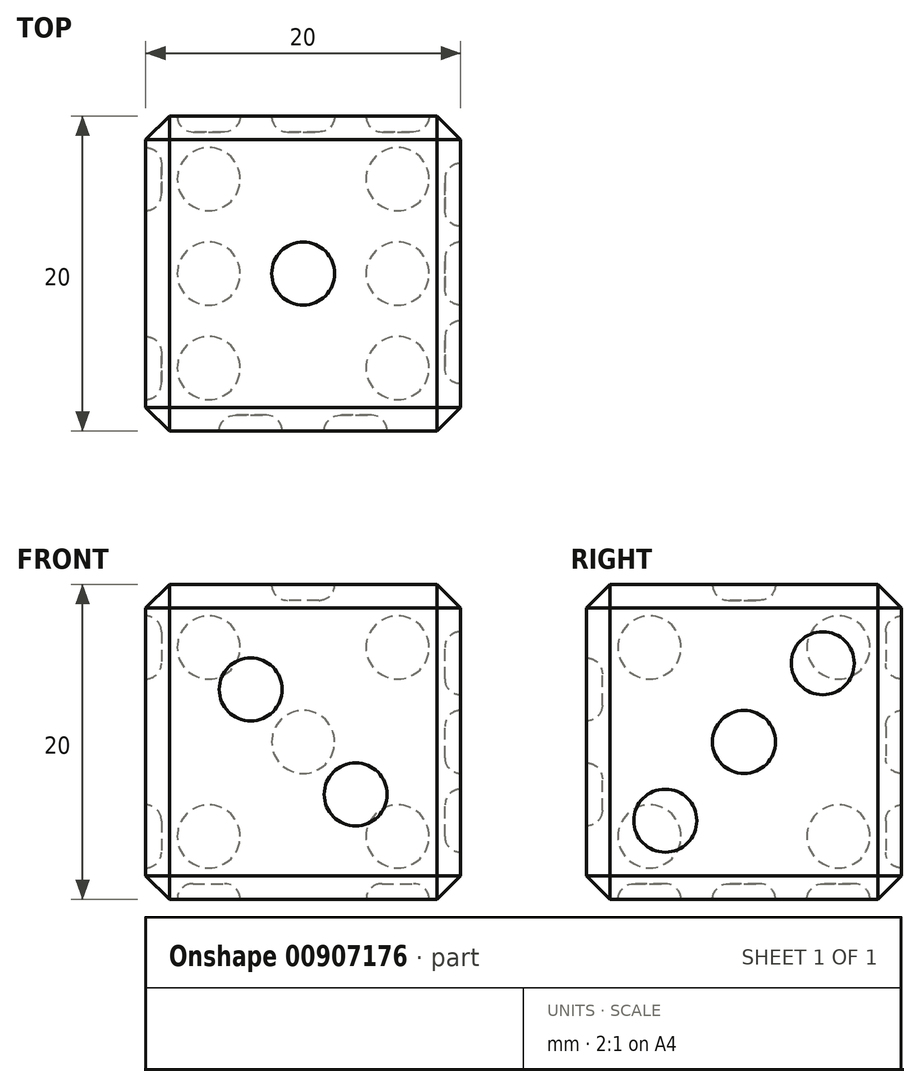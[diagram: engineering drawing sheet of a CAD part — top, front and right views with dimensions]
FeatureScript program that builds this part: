
annotation { "Feature Type Name" : "Feature", "Feature Type Description" : "" }
export const myFeature = defineFeature(function(context is Context, id is Id, definition is map)
    precondition{}
    {
        {
            var Q0;
            Q0=qCreatedBy(makeId("Top.planeOp"),FACE);
            var sketch = newSketch(context, id + "F0", { "sketchPlane" : qUnion([Q0])});
            skLineSegment(sketch, "E0.bottom", {"start": v(0, 0) * mm, "end": v(20, 0) * mm});
            skLineSegment(sketch, "E0.top", {"start": v(0, 20) * mm, "end": v(20, 20) * mm});
            skLineSegment(sketch, "E0.left", {"start": v(0, 0) * mm, "end": v(0, 20) * mm});
            skLineSegment(sketch, "E0.right", {"start": v(20, 0) * mm, "end": v(20, 20) * mm});
            skSolve(sketch);
        }
        {
            var Q0;
            Q0=makeQuery(id+"F0.imprint","IMPRINT",FACE,{"disambiguationData":[TD([[makeQuery(id+"F0.imprint","IMPRINT",EDGE,{"derivedFrom":sQuery(id+"F0.wireOp",EDGE,"E0.bottom")}),1.0]])]});
            extrude(context, id + "F1", {"entities" : qUnion([Q0]), "depth" : 20 * mm, "offsetDistance" : 25 * mm});
        }
        {
            var Q0;
            Q0=makeQuery(id+"F1.opExtrude","CAP_FACE",FACE,{"disambiguationData":[OSD([sQuery(id+"F0.wireOp",EDGE,"E0.bottom"),sQuery(id+"F0.wireOp",EDGE,"E0.top"),sQuery(id+"F0.wireOp",EDGE,"E0.left"),sQuery(id+"F0.wireOp",EDGE,"E0.right")])],"isStart":false});
            var sketch = newSketch(context, id + "F2", { "sketchPlane" : qUnion([Q0])});
            skLineSegment(sketch, "E1", {"start": v(0, 20) * mm, "end": v(20, 0) * mm, "construction": true});
            skLineSegment(sketch, "E2", {"start": v(20, 20) * mm, "end": v(0, 0) * mm, "construction": true});
            skCircle(sketch, "E3", {"center": v(10, 10) * mm, "radius": 2 * mm});
            skSolve(sketch);
        }
        {
            var Q0;
            Q0=makeQuery(id+"F1.opExtrude","CAP_FACE",FACE,{"disambiguationData":[OSD([sQuery(id+"F0.wireOp",EDGE,"E0.bottom"),sQuery(id+"F0.wireOp",EDGE,"E0.top"),sQuery(id+"F0.wireOp",EDGE,"E0.left"),sQuery(id+"F0.wireOp",EDGE,"E0.right")])],"isStart":true});
            var sketch = newSketch(context, id + "F3", { "sketchPlane" : qUnion([Q0])});
            skLineSegment(sketch, "E4", {"start": v(20, -20) * mm, "end": v(0, 0) * mm, "construction": true});
            skLineSegment(sketch, "E5", {"start": v(0, -20) * mm, "end": v(20, 0) * mm, "construction": true});
            skLineSegment(sketch, "E6.bottom", {"start": v(4, -16) * mm, "end": v(16, -16) * mm, "construction": true});
            skLineSegment(sketch, "E6.top", {"start": v(4, -4) * mm, "end": v(16, -4) * mm, "construction": true});
            skLineSegment(sketch, "E6.left", {"start": v(4, -16) * mm, "end": v(4, -4) * mm, "construction": true});
            skLineSegment(sketch, "E6.right", {"start": v(16, -16) * mm, "end": v(16, -4) * mm, "construction": true});
            skPoint(sketch, "E6.middle", {"position": v(10, -10) * mm});
            skCircle(sketch, "E7", {"center": v(4, -16) * mm, "radius": 2 * mm});
            skCircle(sketch, "E8", {"center": v(4, -4) * mm, "radius": 2 * mm});
            skCircle(sketch, "E9", {"center": v(16, -4) * mm, "radius": 2 * mm});
            skCircle(sketch, "E10", {"center": v(16, -16) * mm, "radius": 2 * mm});
            skCircle(sketch, "E11", {"center": v(16, -10) * mm, "radius": 2 * mm});
            skCircle(sketch, "E12", {"center": v(4, -10) * mm, "radius": 2 * mm});
            skSolve(sketch);
        }
        {
            var Q0;
            Q0=makeQuery(id+"F1.opExtrude","SWEPT_FACE",FACE,{"disambiguationData":[OSD([sQuery(id+"F0.wireOp",EDGE,"E0.bottom")])]});
            var sketch = newSketch(context, id + "F4", { "sketchPlane" : qUnion([Q0])});
            skCircle(sketch, "E13", {"center": v(6.67, 13.33) * mm, "radius": 2 * mm});
            skCircle(sketch, "E14", {"center": v(13.33, 6.67) * mm, "radius": 2 * mm});
            skLineSegment(sketch, "E15", {"start": v(20, 0) * mm, "end": v(13.33, 6.67) * mm, "construction": true});
            skLineSegment(sketch, "E16", {"start": v(13.33, 6.67) * mm, "end": v(6.67, 13.33) * mm, "construction": true});
            skLineSegment(sketch, "E17", {"start": v(6.67, 13.33) * mm, "end": v(0, 20) * mm, "construction": true});
            skSolve(sketch);
        }
        {
            var Q0;
            Q0=makeQuery(id+"F1.opExtrude","SWEPT_FACE",FACE,{"disambiguationData":[OSD([sQuery(id+"F0.wireOp",EDGE,"E0.top")])]});
            var sketch = newSketch(context, id + "F5", { "sketchPlane" : qUnion([Q0])});
            skLineSegment(sketch, "E18", {"start": v(0, 20) * mm, "end": v(-20, 0) * mm, "construction": true});
            skLineSegment(sketch, "E19", {"start": v(0, 0) * mm, "end": v(-20, 20) * mm, "construction": true});
            skLineSegment(sketch, "E20.bottom", {"start": v(-4, 16) * mm, "end": v(-16, 16) * mm, "construction": true});
            skLineSegment(sketch, "E20.top", {"start": v(-4, 4) * mm, "end": v(-16, 4) * mm, "construction": true});
            skLineSegment(sketch, "E20.left", {"start": v(-4, 16) * mm, "end": v(-4, 4) * mm, "construction": true});
            skLineSegment(sketch, "E20.right", {"start": v(-16, 16) * mm, "end": v(-16, 4) * mm, "construction": true});
            skPoint(sketch, "E20.middle", {"position": v(-10, 10) * mm});
            skCircle(sketch, "E21", {"center": v(-4, 16) * mm, "radius": 2 * mm});
            skCircle(sketch, "E22", {"center": v(-4, 4) * mm, "radius": 2 * mm});
            skCircle(sketch, "E23", {"center": v(-10, 10) * mm, "radius": 2 * mm});
            skCircle(sketch, "E24", {"center": v(-16, 16) * mm, "radius": 2 * mm});
            skCircle(sketch, "E25", {"center": v(-16, 4) * mm, "radius": 2 * mm});
            skSolve(sketch);
        }
        {
            var Q0;
            Q0=makeQuery(id+"F1.opExtrude","SWEPT_FACE",FACE,{"disambiguationData":[OSD([sQuery(id+"F0.wireOp",EDGE,"E0.right")])]});
            var sketch = newSketch(context, id + "F6", { "sketchPlane" : qUnion([Q0])});
            skCircle(sketch, "E26", {"center": v(15, 15) * mm, "radius": 2 * mm});
            skCircle(sketch, "E27", {"center": v(10, 10) * mm, "radius": 2 * mm});
            skCircle(sketch, "E28", {"center": v(5, 5) * mm, "radius": 2 * mm});
            skLineSegment(sketch, "E29", {"start": v(0, 0) * mm, "end": v(5, 5) * mm, "construction": true});
            skLineSegment(sketch, "E30", {"start": v(10, 10) * mm, "end": v(5, 5) * mm, "construction": true});
            skLineSegment(sketch, "E31", {"start": v(10, 10) * mm, "end": v(15, 15) * mm, "construction": true});
            skLineSegment(sketch, "E32", {"start": v(15, 15) * mm, "end": v(20, 20) * mm, "construction": true});
            skSolve(sketch);
        }
        {
            var Q0;
            Q0=makeQuery(id+"F1.opExtrude","SWEPT_FACE",FACE,{"disambiguationData":[OSD([sQuery(id+"F0.wireOp",EDGE,"E0.left")])]});
            var sketch = newSketch(context, id + "F7", { "sketchPlane" : qUnion([Q0])});
            skLineSegment(sketch, "E33", {"start": v(-20, 20) * mm, "end": v(0, 0) * mm, "construction": true});
            skLineSegment(sketch, "E34", {"start": v(0, 20) * mm, "end": v(-20, 0) * mm, "construction": true});
            skLineSegment(sketch, "E35.bottom", {"start": v(-16, 16) * mm, "end": v(-4, 16) * mm, "construction": true});
            skLineSegment(sketch, "E35.top", {"start": v(-16, 4) * mm, "end": v(-4, 4) * mm, "construction": true});
            skLineSegment(sketch, "E35.left", {"start": v(-16, 16) * mm, "end": v(-16, 4) * mm, "construction": true});
            skLineSegment(sketch, "E35.right", {"start": v(-4, 16) * mm, "end": v(-4, 4) * mm, "construction": true});
            skPoint(sketch, "E35.middle", {"position": v(-10, 10) * mm});
            skCircle(sketch, "E36", {"center": v(-16, 16) * mm, "radius": 2 * mm});
            skCircle(sketch, "E37", {"center": v(-16, 4) * mm, "radius": 2 * mm});
            skCircle(sketch, "E38", {"center": v(-4, 4) * mm, "radius": 2 * mm});
            skCircle(sketch, "E39", {"center": v(-4, 16) * mm, "radius": 2 * mm});
            skSolve(sketch);
        }
        {
            var Q0;
            Q0=makeQuery(id+"F5.imprint","IMPRINT",FACE,{"disambiguationData":[TD([[makeQuery(id+"F5.imprint","IMPRINT",EDGE,{"derivedFrom":sQuery(id+"F5.wireOp",EDGE,"E24")}),1.0]])]});
            var Q1;
            Q1=makeQuery(id+"F5.imprint","IMPRINT",FACE,{"disambiguationData":[TD([[makeQuery(id+"F5.imprint","IMPRINT",EDGE,{"derivedFrom":sQuery(id+"F5.wireOp",EDGE,"E21")}),1.0]])]});
            var Q2;
            Q2=makeQuery(id+"F5.imprint","IMPRINT",FACE,{"disambiguationData":[TD([[makeQuery(id+"F5.imprint","IMPRINT",EDGE,{"derivedFrom":sQuery(id+"F5.wireOp",EDGE,"E23")}),1.0]])]});
            var Q3;
            Q3=makeQuery(id+"F5.imprint","IMPRINT",FACE,{"disambiguationData":[TD([[makeQuery(id+"F5.imprint","IMPRINT",EDGE,{"derivedFrom":sQuery(id+"F5.wireOp",EDGE,"E22")}),1.0]])]});
            var Q4;
            Q4=makeQuery(id+"F5.imprint","IMPRINT",FACE,{"disambiguationData":[TD([[makeQuery(id+"F5.imprint","IMPRINT",EDGE,{"derivedFrom":sQuery(id+"F5.wireOp",EDGE,"E25")}),1.0]])]});
            extrude(context, id + "F8", {"entities" : qUnion([Q0, Q1, Q2, Q3, Q4]), "operationType" : NewBodyOperationType.REMOVE, "oppositeDirection" : true, "depth" : 1 * mm, "offsetDistance" : 25 * mm});
        }
        {
            var Q0;
            Q0=makeQuery(id+"F2.imprint","IMPRINT",FACE,{"disambiguationData":[TD([[makeQuery(id+"F2.imprint","IMPRINT",EDGE,{"derivedFrom":sQuery(id+"F2.wireOp",EDGE,"E3")}),1.0]])]});
            extrude(context, id + "F9", {"entities" : qUnion([Q0]), "operationType" : NewBodyOperationType.REMOVE, "oppositeDirection" : true, "depth" : 1 * mm, "offsetDistance" : 25 * mm});
        }
        {
            var Q0;
            Q0=makeQuery(id+"F3.imprint","IMPRINT",FACE,{"disambiguationData":[TD([[makeQuery(id+"F3.imprint","IMPRINT",EDGE,{"derivedFrom":sQuery(id+"F3.wireOp",EDGE,"E10")}),1.0]])]});
            var Q1;
            Q1=makeQuery(id+"F3.imprint","IMPRINT",FACE,{"disambiguationData":[TD([[makeQuery(id+"F3.imprint","IMPRINT",EDGE,{"derivedFrom":sQuery(id+"F3.wireOp",EDGE,"E11")}),1.0]])]});
            var Q2;
            Q2=makeQuery(id+"F3.imprint","IMPRINT",FACE,{"disambiguationData":[TD([[makeQuery(id+"F3.imprint","IMPRINT",EDGE,{"derivedFrom":sQuery(id+"F3.wireOp",EDGE,"E9")}),1.0]])]});
            var Q3;
            Q3=makeQuery(id+"F3.imprint","IMPRINT",FACE,{"disambiguationData":[TD([[makeQuery(id+"F3.imprint","IMPRINT",EDGE,{"derivedFrom":sQuery(id+"F3.wireOp",EDGE,"E8")}),1.0]])]});
            var Q4;
            Q4=makeQuery(id+"F3.imprint","IMPRINT",FACE,{"disambiguationData":[TD([[makeQuery(id+"F3.imprint","IMPRINT",EDGE,{"derivedFrom":sQuery(id+"F3.wireOp",EDGE,"E12")}),1.0]])]});
            var Q5;
            Q5=makeQuery(id+"F3.imprint","IMPRINT",FACE,{"disambiguationData":[TD([[makeQuery(id+"F3.imprint","IMPRINT",EDGE,{"derivedFrom":sQuery(id+"F3.wireOp",EDGE,"E7")}),1.0]])]});
            extrude(context, id + "F10", {"entities" : qUnion([Q0, Q1, Q2, Q3, Q4, Q5]), "operationType" : NewBodyOperationType.REMOVE, "oppositeDirection" : true, "depth" : 1 * mm, "offsetDistance" : 25 * mm});
        }
        {
            var Q0;
            Q0=makeQuery(id+"F7.imprint","IMPRINT",FACE,{"disambiguationData":[TD([[makeQuery(id+"F7.imprint","IMPRINT",EDGE,{"derivedFrom":sQuery(id+"F7.wireOp",EDGE,"E37")}),1.0]])]});
            var Q1;
            Q1=makeQuery(id+"F7.imprint","IMPRINT",FACE,{"disambiguationData":[TD([[makeQuery(id+"F7.imprint","IMPRINT",EDGE,{"derivedFrom":sQuery(id+"F7.wireOp",EDGE,"E36")}),1.0]])]});
            var Q2;
            Q2=makeQuery(id+"F7.imprint","IMPRINT",FACE,{"disambiguationData":[TD([[makeQuery(id+"F7.imprint","IMPRINT",EDGE,{"derivedFrom":sQuery(id+"F7.wireOp",EDGE,"E39")}),1.0]])]});
            var Q3;
            Q3=makeQuery(id+"F7.imprint","IMPRINT",FACE,{"disambiguationData":[TD([[makeQuery(id+"F7.imprint","IMPRINT",EDGE,{"derivedFrom":sQuery(id+"F7.wireOp",EDGE,"E38")}),1.0]])]});
            extrude(context, id + "F11", {"entities" : qUnion([Q0, Q1, Q2, Q3]), "operationType" : NewBodyOperationType.REMOVE, "oppositeDirection" : true, "depth" : 1 * mm, "offsetDistance" : 25 * mm});
        }
        {
            var Q0;
            Q0=makeQuery(id+"F4.imprint","IMPRINT",FACE,{"disambiguationData":[TD([[makeQuery(id+"F4.imprint","IMPRINT",EDGE,{"derivedFrom":sQuery(id+"F4.wireOp",EDGE,"E14")}),1.0]])]});
            var Q1;
            Q1=makeQuery(id+"F4.imprint","IMPRINT",FACE,{"disambiguationData":[TD([[makeQuery(id+"F4.imprint","IMPRINT",EDGE,{"derivedFrom":sQuery(id+"F4.wireOp",EDGE,"E13")}),1.0]])]});
            extrude(context, id + "F12", {"entities" : qUnion([Q0, Q1]), "operationType" : NewBodyOperationType.REMOVE, "oppositeDirection" : true, "depth" : 1 * mm, "offsetDistance" : 25 * mm});
        }
        {
            var Q0;
            Q0=makeQuery(id+"F6.imprint","IMPRINT",FACE,{"disambiguationData":[TD([[makeQuery(id+"F6.imprint","IMPRINT",EDGE,{"derivedFrom":sQuery(id+"F6.wireOp",EDGE,"E26")}),1.0]])]});
            var Q1;
            Q1=makeQuery(id+"F6.imprint","IMPRINT",FACE,{"disambiguationData":[TD([[makeQuery(id+"F6.imprint","IMPRINT",EDGE,{"derivedFrom":sQuery(id+"F6.wireOp",EDGE,"E27")}),1.0]])]});
            var Q2;
            Q2=makeQuery(id+"F6.imprint","IMPRINT",FACE,{"disambiguationData":[TD([[makeQuery(id+"F6.imprint","IMPRINT",EDGE,{"derivedFrom":sQuery(id+"F6.wireOp",EDGE,"E28")}),1.0]])]});
            extrude(context, id + "F13", {"entities" : qUnion([Q0, Q1, Q2]), "operationType" : NewBodyOperationType.REMOVE, "oppositeDirection" : true, "depth" : 1 * mm, "offsetDistance" : 25 * mm});
        }
        {
            var Q0;
            Q0=makeQuery(id+"F1.opExtrude","CAP_EDGE",EDGE,{"disambiguationData":[OSD([sQuery(id+"F0.wireOp",EDGE,"E0.right")])],"isStart":false});
            var Q1;
            Q1=makeQuery(id+"F1.opExtrude","SWEPT_EDGE",EDGE,{"disambiguationData":[OSD([sQuery(id+"F0.wireOp",EDGE,"E0.bottom"),sQuery(id+"F0.wireOp",EDGE,"E0.right")])]});
            var Q2;
            Q2=makeQuery(id+"F1.opExtrude","SWEPT_EDGE",EDGE,{"disambiguationData":[OSD([sQuery(id+"F0.wireOp",EDGE,"E0.top"),sQuery(id+"F0.wireOp",EDGE,"E0.right")])]});
            var Q3;
            Q3=makeQuery(id+"F1.opExtrude","CAP_EDGE",EDGE,{"disambiguationData":[OSD([sQuery(id+"F0.wireOp",EDGE,"E0.right")])],"isStart":true});
            var Q4;
            Q4=makeQuery(id+"F1.opExtrude","CAP_EDGE",EDGE,{"disambiguationData":[OSD([sQuery(id+"F0.wireOp",EDGE,"E0.bottom")])],"isStart":true});
            var Q5;
            Q5=makeQuery(id+"F1.opExtrude","CAP_EDGE",EDGE,{"disambiguationData":[OSD([sQuery(id+"F0.wireOp",EDGE,"E0.top")])],"isStart":true});
            var Q6;
            Q6=makeQuery(id+"F1.opExtrude","CAP_EDGE",EDGE,{"disambiguationData":[OSD([sQuery(id+"F0.wireOp",EDGE,"E0.left")])],"isStart":true});
            var Q7;
            Q7=makeQuery(id+"F1.opExtrude","SWEPT_EDGE",EDGE,{"disambiguationData":[OSD([sQuery(id+"F0.wireOp",EDGE,"E0.bottom"),sQuery(id+"F0.wireOp",EDGE,"E0.left")])]});
            var Q8;
            Q8=makeQuery(id+"F1.opExtrude","CAP_EDGE",EDGE,{"disambiguationData":[OSD([sQuery(id+"F0.wireOp",EDGE,"E0.bottom")])],"isStart":false});
            var Q9;
            Q9=makeQuery(id+"F1.opExtrude","CAP_EDGE",EDGE,{"disambiguationData":[OSD([sQuery(id+"F0.wireOp",EDGE,"E0.top")])],"isStart":false});
            var Q10;
            Q10=makeQuery(id+"F1.opExtrude","SWEPT_EDGE",EDGE,{"disambiguationData":[OSD([sQuery(id+"F0.wireOp",EDGE,"E0.top"),sQuery(id+"F0.wireOp",EDGE,"E0.left")])]});
            var Q11;
            Q11=makeQuery(id+"F1.opExtrude","CAP_EDGE",EDGE,{"disambiguationData":[OSD([sQuery(id+"F0.wireOp",EDGE,"E0.left")])],"isStart":false});
            chamfer(context, id + "F14", {"entities" : qUnion([Q0, Q1, Q2, Q3, Q4, Q5, Q6, Q7, Q8, Q9, Q10, Q11]), "width" : 1.5 * mm, "tangentPropagation" : true});
        }
        {
            var Q0;
            Q0=makeQuery(id+"F8.boolean.opBoolean","COPY",EDGE,{"derivedFrom":makeQuery(id+"F8.opExtrude","CAP_EDGE",EDGE,{"disambiguationData":[OSD([sQuery(id+"F5.wireOp",EDGE,"E21")])],"isStart":false})});
            var Q1;
            Q1=makeQuery(id+"F8.boolean.opBoolean","COPY",EDGE,{"derivedFrom":makeQuery(id+"F8.opExtrude","CAP_EDGE",EDGE,{"disambiguationData":[OSD([sQuery(id+"F5.wireOp",EDGE,"E23")])],"isStart":false})});
            var Q2;
            Q2=makeQuery(id+"F8.boolean.opBoolean","COPY",EDGE,{"derivedFrom":makeQuery(id+"F8.opExtrude","CAP_EDGE",EDGE,{"disambiguationData":[OSD([sQuery(id+"F5.wireOp",EDGE,"E24")])],"isStart":false})});
            var Q3;
            Q3=makeQuery(id+"F8.boolean.opBoolean","COPY",EDGE,{"derivedFrom":makeQuery(id+"F8.opExtrude","CAP_EDGE",EDGE,{"disambiguationData":[OSD([sQuery(id+"F5.wireOp",EDGE,"E25")])],"isStart":false})});
            var Q4;
            Q4=makeQuery(id+"F8.boolean.opBoolean","COPY",EDGE,{"derivedFrom":makeQuery(id+"F8.opExtrude","CAP_EDGE",EDGE,{"disambiguationData":[OSD([sQuery(id+"F5.wireOp",EDGE,"E22")])],"isStart":false})});
            var Q5;
            Q5=makeQuery(id+"F13.boolean.opBoolean","COPY",EDGE,{"derivedFrom":makeQuery(id+"F13.opExtrude","CAP_EDGE",EDGE,{"disambiguationData":[OSD([sQuery(id+"F6.wireOp",EDGE,"E26")])],"isStart":false})});
            var Q6;
            Q6=makeQuery(id+"F13.boolean.opBoolean","COPY",EDGE,{"derivedFrom":makeQuery(id+"F13.opExtrude","CAP_EDGE",EDGE,{"disambiguationData":[OSD([sQuery(id+"F6.wireOp",EDGE,"E27")])],"isStart":false})});
            var Q7;
            Q7=makeQuery(id+"F13.boolean.opBoolean","COPY",EDGE,{"derivedFrom":makeQuery(id+"F13.opExtrude","CAP_EDGE",EDGE,{"disambiguationData":[OSD([sQuery(id+"F6.wireOp",EDGE,"E28")])],"isStart":false})});
            var Q8;
            Q8=makeQuery(id+"F9.boolean.opBoolean","COPY",EDGE,{"derivedFrom":makeQuery(id+"F9.opExtrude","CAP_EDGE",EDGE,{"disambiguationData":[OSD([sQuery(id+"F2.wireOp",EDGE,"E3")])],"isStart":false})});
            var Q9;
            Q9=makeQuery(id+"F11.boolean.opBoolean","COPY",EDGE,{"derivedFrom":makeQuery(id+"F11.opExtrude","CAP_EDGE",EDGE,{"disambiguationData":[OSD([sQuery(id+"F7.wireOp",EDGE,"E36")])],"isStart":false})});
            var Q10;
            Q10=makeQuery(id+"F11.boolean.opBoolean","COPY",EDGE,{"derivedFrom":makeQuery(id+"F11.opExtrude","CAP_EDGE",EDGE,{"disambiguationData":[OSD([sQuery(id+"F7.wireOp",EDGE,"E37")])],"isStart":false})});
            var Q11;
            Q11=makeQuery(id+"F11.boolean.opBoolean","COPY",EDGE,{"derivedFrom":makeQuery(id+"F11.opExtrude","CAP_EDGE",EDGE,{"disambiguationData":[OSD([sQuery(id+"F7.wireOp",EDGE,"E38")])],"isStart":false})});
            var Q12;
            Q12=makeQuery(id+"F11.boolean.opBoolean","COPY",EDGE,{"derivedFrom":makeQuery(id+"F11.opExtrude","CAP_EDGE",EDGE,{"disambiguationData":[OSD([sQuery(id+"F7.wireOp",EDGE,"E39")])],"isStart":false})});
            var Q13;
            Q13=makeQuery(id+"F12.boolean.opBoolean","COPY",EDGE,{"derivedFrom":makeQuery(id+"F12.opExtrude","CAP_EDGE",EDGE,{"disambiguationData":[OSD([sQuery(id+"F4.wireOp",EDGE,"E13")])],"isStart":false})});
            var Q14;
            Q14=makeQuery(id+"F12.boolean.opBoolean","COPY",EDGE,{"derivedFrom":makeQuery(id+"F12.opExtrude","CAP_EDGE",EDGE,{"disambiguationData":[OSD([sQuery(id+"F4.wireOp",EDGE,"E14")])],"isStart":false})});
            var Q15;
            Q15=makeQuery(id+"F10.boolean.opBoolean","COPY",EDGE,{"derivedFrom":makeQuery(id+"F10.opExtrude","CAP_EDGE",EDGE,{"disambiguationData":[OSD([sQuery(id+"F3.wireOp",EDGE,"E8")])],"isStart":false})});
            var Q16;
            Q16=makeQuery(id+"F10.boolean.opBoolean","COPY",EDGE,{"derivedFrom":makeQuery(id+"F10.opExtrude","CAP_EDGE",EDGE,{"disambiguationData":[OSD([sQuery(id+"F3.wireOp",EDGE,"E12")])],"isStart":false})});
            var Q17;
            Q17=makeQuery(id+"F10.boolean.opBoolean","COPY",EDGE,{"derivedFrom":makeQuery(id+"F10.opExtrude","CAP_EDGE",EDGE,{"disambiguationData":[OSD([sQuery(id+"F3.wireOp",EDGE,"E7")])],"isStart":false})});
            var Q18;
            Q18=makeQuery(id+"F10.boolean.opBoolean","COPY",EDGE,{"derivedFrom":makeQuery(id+"F10.opExtrude","CAP_EDGE",EDGE,{"disambiguationData":[OSD([sQuery(id+"F3.wireOp",EDGE,"E10")])],"isStart":false})});
            var Q19;
            Q19=makeQuery(id+"F10.boolean.opBoolean","COPY",EDGE,{"derivedFrom":makeQuery(id+"F10.opExtrude","CAP_EDGE",EDGE,{"disambiguationData":[OSD([sQuery(id+"F3.wireOp",EDGE,"E11")])],"isStart":false})});
            var Q20;
            Q20=makeQuery(id+"F10.boolean.opBoolean","COPY",EDGE,{"derivedFrom":makeQuery(id+"F10.opExtrude","CAP_EDGE",EDGE,{"disambiguationData":[OSD([sQuery(id+"F3.wireOp",EDGE,"E9")])],"isStart":false})});
            fillet(context, id + "F15", {"entities" : qUnion([Q0, Q1, Q2, Q3, Q4, Q5, Q6, Q7, Q8, Q9, Q10, Q11, Q12, Q13, Q14, Q15, Q16, Q17, Q18, Q19, Q20]), "radius" : 1 * mm, "tangentPropagation" : true, "allowEdgeOverflow" : false});
        }
    });
